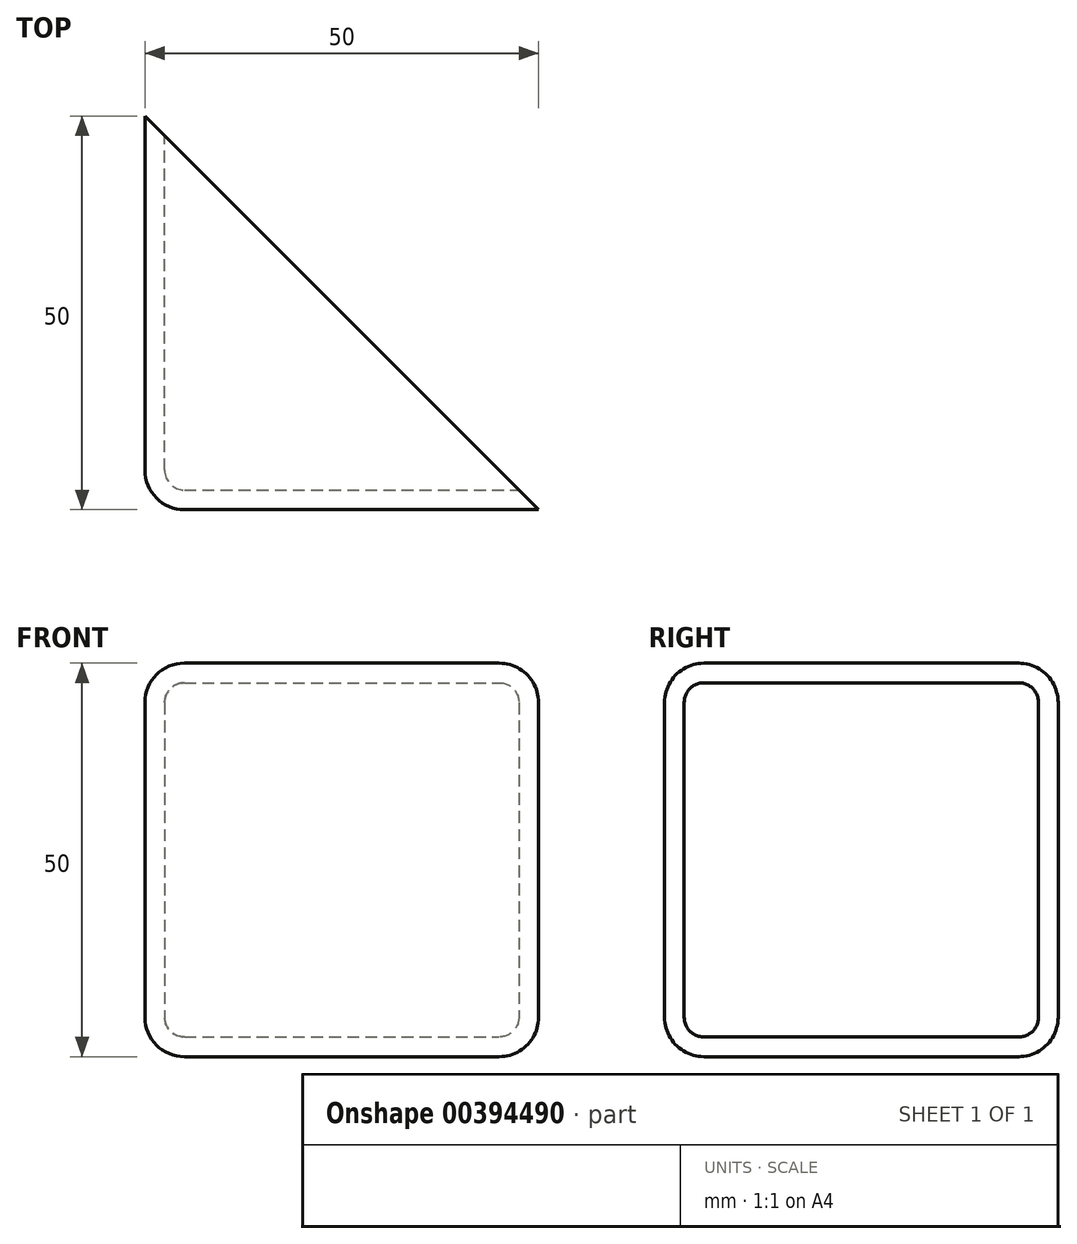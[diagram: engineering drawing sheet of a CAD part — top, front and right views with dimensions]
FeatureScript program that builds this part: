
annotation { "Feature Type Name" : "Feature", "Feature Type Description" : "" }
export const myFeature = defineFeature(function(context is Context, id is Id, definition is map)
    precondition{}
    {
        {
            var Q0;
            Q0=qCreatedBy(makeId("Top.planeOp"),FACE);
            var sketch = newSketch(context, id + "F0", { "sketchPlane" : qUnion([Q0])});
            skLineSegment(sketch, "E0.bottom", {"start": v(-4.14, -4.18) * mm, "end": v(45.86, -4.18) * mm});
            skLineSegment(sketch, "E0.left", {"start": v(-4.14, -4.18) * mm, "end": v(-4.14, 45.82) * mm});
            skLineSegment(sketch, "E1", {"start": v(-4.14, 45.82) * mm, "end": v(45.86, -4.18) * mm});
            skSolve(sketch);
        }
        {
            var Q0;
            Q0 = qSketchRegion(id + "F0", true);
            extrude(context, id + "F1", {"entities" : qUnion([Q0]), "depth" : 50 * mm});
        }
        {
            var Q0;
            Q0=makeQuery(id+"F1.opExtrude","SWEPT_EDGE",EDGE,{"disambiguationData":[OSD([sQuery(id+"F0.wireOp",EDGE,"E0.bottom"),sQuery(id+"F0.wireOp",EDGE,"E0.left")])]});
            var Q1;
            Q1=makeQuery(id+"F1.opExtrude","CAP_EDGE",EDGE,{"disambiguationData":[OSD([sQuery(id+"F0.wireOp",EDGE,"E0.bottom")])],"isStart":true});
            var Q2;
            Q2=makeQuery(id+"F1.opExtrude","CAP_EDGE",EDGE,{"disambiguationData":[OSD([sQuery(id+"F0.wireOp",EDGE,"E0.left")])],"isStart":true});
            var Q3;
            Q3=makeQuery(id+"F1.opExtrude","CAP_EDGE",EDGE,{"disambiguationData":[OSD([sQuery(id+"F0.wireOp",EDGE,"E0.left")])],"isStart":false});
            var Q4;
            Q4=makeQuery(id+"F1.opExtrude","CAP_EDGE",EDGE,{"disambiguationData":[OSD([sQuery(id+"F0.wireOp",EDGE,"E0.bottom")])],"isStart":false});
            fillet(context, id + "F2", {"entities" : qUnion([Q0, Q1, Q2, Q3, Q4]), "radius" : 5 * mm, "tangentPropagation" : true, "allowEdgeOverflow" : false});
        }
        {
            var Q0;
            Q0=makeQuery(id+"F1.opExtrude","SWEPT_FACE",FACE,{"disambiguationData":[OSD([sQuery(id+"F0.wireOp",EDGE,"E1")])]});
            shell(context, id + "F3", {"entities" : qUnion([Q0]), "thickness" : 2.5 * mm});
        }
    });
